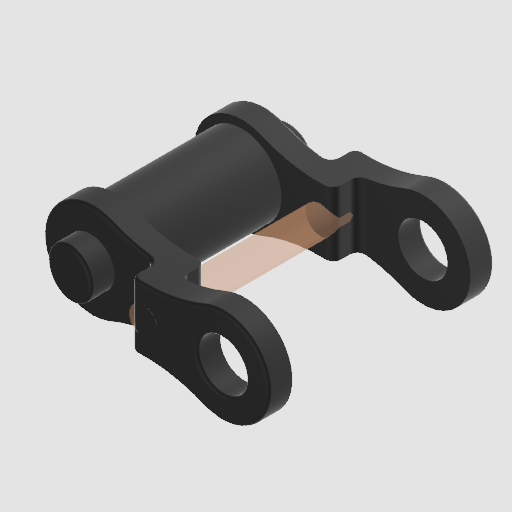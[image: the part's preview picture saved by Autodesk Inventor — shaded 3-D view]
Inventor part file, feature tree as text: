
AUTODESK INVENTOR PART (.ipt)
format: ipt  version: 2021 (Build 250183000, 183)  size: 671,744 bytes
history: native  units: in
note: dims shown in document units (in); Inventor stores cm internally (conversion verified against a paired STEP export)
features: other x4, sketch x3, extrude x3, imported_body x1, plane x1
ambient origin geometry x8: Origin, YZ Plane, XZ Plane, XY Plane, X Axis, Y Axis, Z Axis, Center Point
bodies: Body1 (feature_tree), Body2 (feature_tree), Body3 (feature_tree), Body4 (feature_tree)
feature tree (12):
  parser-record x1  (decoder bookkeeping rows leaked as tree rows — omitted from the tree; the rows remain in map.json)
  imported_body  "Base1"
  plane  "XZ Plane2"
  sketch  "Sketch1"  dims[d0=0.118in d1=0.063in d2=0.0in]
  other  "Srf1"
  sketch  "Sketch2"  dims[d3=0.0in d4=0.118in]
  other  "Srf2"
  sketch  "Sketch3"  dims[d5=0.063in d6=0.0in d7=0.0in d13=0.1575in d14=0.0in d15=0.559in d16=0.0in]
  other  "Srf3"
  extrude  "ExtrusionSrf1"  Depth=0.118in TaperAngle=0.0deg
  extrude  "ExtrusionSrf2"  Depth=0.118in
  extrude  "ExtrusionSrf3"  TaperAngle=0.0deg  [1 undecoded]
note: 1 required parameter value undecoded (feature->parameter linkage not recoverable at this tier; creation-order binding heuristic only, values carry confidence <= 0.55)
